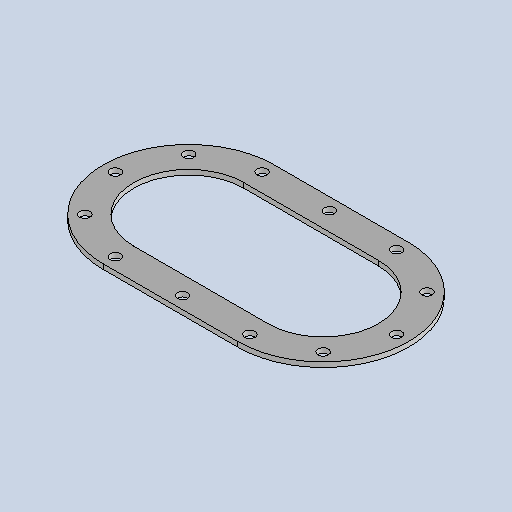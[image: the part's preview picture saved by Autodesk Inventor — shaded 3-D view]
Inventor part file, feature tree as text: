
AUTODESK INVENTOR PART (.ipt)
format: ipt  version: 2025.1 (Build 291241020, 241B)  size: 147,456 bytes
history: native  units: mm
features: sketch x3, other x3, sheet_metal_op x1, pattern_circular x1, mirror x1
ambient origin geometry x8: Origin, YZ Plane, XZ Plane, XY Plane, X Axis, Y Axis, Z Axis, Center Point
bodies: Body1 (feature_tree)
feature tree (9):
  sheet_metal_op  "Face2"
  pattern_circular  "Circular Pattern1"  Count=40  [1 undecoded]
  mirror  "Mirror1"
  sketch  "Sketch2"  dims[d12=180.0mm]
  other  "Plate2"
  sketch  "Sketch3"  dims[d13=50.0mm]
  sketch  "Sketch4"  dims[d14=8.0mm d15=17.0mm d16=20.0mm d17=8.0mm d18=0.0mm d19=50.0mm d20=180.0deg d22=0.0mm d23=8.0mm d24=0.0mm]
  other  "Cut1"
  other  "Cut2"
note: 1 required parameter value undecoded (feature->parameter linkage not recoverable at this tier; creation-order binding heuristic only, values carry confidence <= 0.55)
